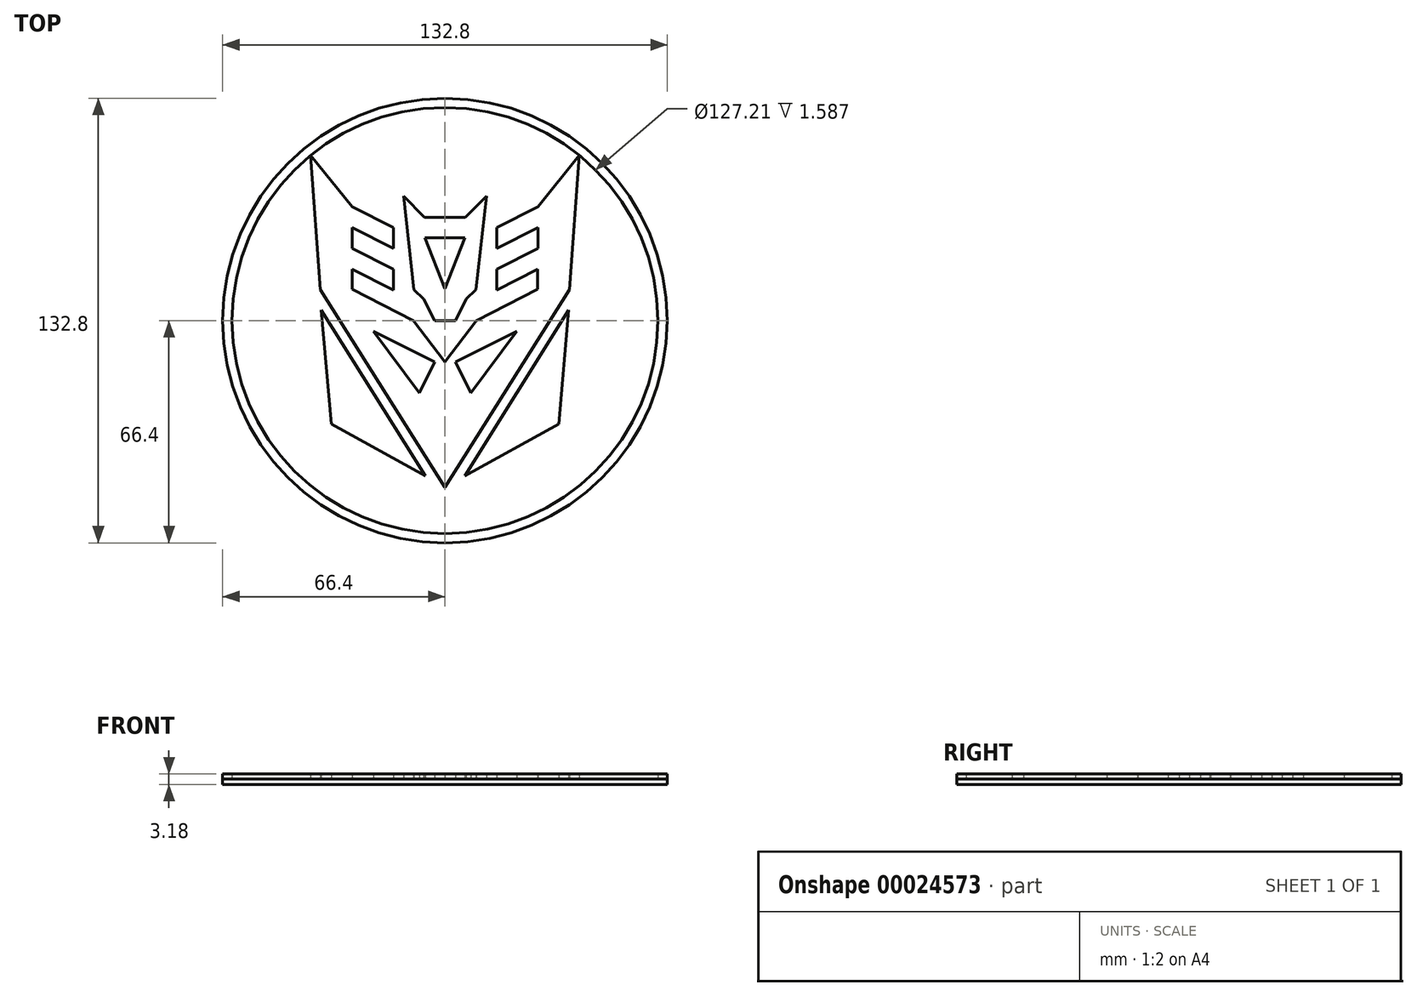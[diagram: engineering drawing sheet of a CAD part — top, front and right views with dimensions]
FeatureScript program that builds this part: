
annotation { "Feature Type Name" : "Feature", "Feature Type Description" : "" }
export const myFeature = defineFeature(function(context is Context, id is Id, definition is map)
    precondition{}
    {
        {
            var Q0;
            Q0=qCreatedBy(makeId("Top.planeOp"),FACE);
            var sketch = newSketch(context, id + "F0", { "sketchPlane" : qUnion([Q0])});
            skCircle(sketch, "E0", {"center": v(0, 0) * mm, "radius": 66.4 * mm});
            skSolve(sketch);
        }
        {
            var Q0;
            Q0 = qSketchRegion(id + "F0", true);
            extrude(context, id + "F1", {"entities" : qUnion([Q0]), "depth" : 1.59 * mm});
        }
        {
            var Q0;
            Q0=makeQuery(id+"F1.opExtrude","CAP_FACE",FACE,{"disambiguationData":[OSD([sQuery(id+"F0.wireOp",EDGE,"E0")])],"isStart":false});
            var sketch = newSketch(context, id + "F2", { "sketchPlane" : qUnion([Q0])});
            skLineSegment(sketch, "E1", {"start": v(-40.14, 49.34) * mm, "end": v(-27.72, 34) * mm});
            skLineSegment(sketch, "E2", {"start": v(-27.72, 34) * mm, "end": v(-15.4, 27.8) * mm});
            skLineSegment(sketch, "E3", {"start": v(-15.4, 27.8) * mm, "end": v(-15.4, 21.53) * mm});
            skLineSegment(sketch, "E4", {"start": v(-15.4, 21.53) * mm, "end": v(-27.77, 27.76) * mm});
            skLineSegment(sketch, "E5", {"start": v(-27.77, 27.76) * mm, "end": v(-27.77, 21.57) * mm});
            skLineSegment(sketch, "E6", {"start": v(-27.77, 21.57) * mm, "end": v(-15.4, 15.39) * mm});
            skLineSegment(sketch, "E7", {"start": v(-15.4, 15.39) * mm, "end": v(-15.4, 9.16) * mm});
            skLineSegment(sketch, "E8", {"start": v(-15.4, 9.16) * mm, "end": v(-27.68, 15.34) * mm});
            skLineSegment(sketch, "E9", {"start": v(-27.68, 15.34) * mm, "end": v(-27.68, 9.35) * mm});
            skLineSegment(sketch, "E10", {"start": v(-27.68, 9.35) * mm, "end": v(-9.4, 0) * mm});
            skLineSegment(sketch, "E11", {"start": v(-9.4, 0) * mm, "end": v(0, -12.37) * mm});
            skLineSegment(sketch, "E12", {"start": v(-40.14, 49.34) * mm, "end": v(-37.2, 9.23) * mm});
            skLineSegment(sketch, "E13", {"start": v(-37.2, 9.23) * mm, "end": v(0, -49.8) * mm});
            skLineSegment(sketch, "E14", {"start": v(-5.9, -46.44) * mm, "end": v(-36.98, 3.08) * mm});
            skLineSegment(sketch, "E15", {"start": v(-36.98, 3.08) * mm, "end": v(-33.96, -30.93) * mm});
            skLineSegment(sketch, "E16", {"start": v(-33.96, -30.93) * mm, "end": v(-5.9, -46.44) * mm});
            skLineSegment(sketch, "E17", {"start": v(-3.08, -12.32) * mm, "end": v(-21.39, -3.2) * mm});
            skLineSegment(sketch, "E18", {"start": v(-21.39, -3.2) * mm, "end": v(-7.68, -21.59) * mm});
            skLineSegment(sketch, "E19", {"start": v(-7.68, -21.59) * mm, "end": v(-3.08, -12.32) * mm});
            skLineSegment(sketch, "E20", {"start": v(0, 0) * mm, "end": v(-3.08, 0) * mm});
            skLineSegment(sketch, "E21", {"start": v(-3.08, 0) * mm, "end": v(-6.35, 6.44) * mm});
            skLineSegment(sketch, "E22", {"start": v(-6.35, 6.44) * mm, "end": v(-9.26, 9.26) * mm});
            skLineSegment(sketch, "E23", {"start": v(-9.26, 9.26) * mm, "end": v(-12.38, 37.13) * mm});
            skLineSegment(sketch, "E24", {"start": v(-12.38, 37.13) * mm, "end": v(-6.1, 30.82) * mm});
            skLineSegment(sketch, "E25", {"start": v(-6.1, 30.82) * mm, "end": v(0, 30.82) * mm});
            skLineSegment(sketch, "E26", {"start": v(0, 9.45) * mm, "end": v(-6, 24.67) * mm});
            skLineSegment(sketch, "E27", {"start": v(-6, 24.67) * mm, "end": v(0, 24.67) * mm});
            skLineSegment(sketch, "E28", {"start": v(0, 0) * mm, "end": v(0, 55.53) * mm, "construction": true});
            skLineSegment(sketch, "E29.MirrorCS", {"start": v(6.35, 6.44) * mm, "end": v(9.26, 9.26) * mm});
            skLineSegment(sketch, "E30.MirrorCS", {"start": v(0, 0) * mm, "end": v(3.08, 0) * mm});
            skLineSegment(sketch, "E31.MirrorCS", {"start": v(15.4, 15.39) * mm, "end": v(15.4, 9.16) * mm});
            skLineSegment(sketch, "E32.MirrorCS", {"start": v(15.4, 9.16) * mm, "end": v(27.68, 15.34) * mm});
            skLineSegment(sketch, "E33.MirrorCS", {"start": v(27.77, 21.57) * mm, "end": v(15.4, 15.39) * mm});
            skLineSegment(sketch, "E34.MirrorCS", {"start": v(27.77, 27.76) * mm, "end": v(27.77, 21.57) * mm});
            skLineSegment(sketch, "E35.MirrorCS", {"start": v(27.68, 15.34) * mm, "end": v(27.68, 9.35) * mm});
            skLineSegment(sketch, "E36.MirrorCS", {"start": v(15.4, 21.53) * mm, "end": v(27.77, 27.76) * mm});
            skLineSegment(sketch, "E37.MirrorCS", {"start": v(27.68, 9.35) * mm, "end": v(9.4, 0) * mm});
            skLineSegment(sketch, "E38.MirrorCS", {"start": v(15.4, 27.8) * mm, "end": v(15.4, 21.53) * mm});
            skLineSegment(sketch, "E39.MirrorCS", {"start": v(27.72, 34) * mm, "end": v(15.4, 27.8) * mm});
            skLineSegment(sketch, "E40.MirrorCS", {"start": v(9.4, 0) * mm, "end": v(0, -12.37) * mm});
            skLineSegment(sketch, "E41.MirrorCS", {"start": v(40.14, 49.34) * mm, "end": v(27.72, 34) * mm});
            skLineSegment(sketch, "E42.MirrorCS", {"start": v(33.96, -30.93) * mm, "end": v(5.9, -46.44) * mm});
            skLineSegment(sketch, "E43.MirrorCS", {"start": v(40.14, 49.34) * mm, "end": v(37.2, 9.23) * mm});
            skLineSegment(sketch, "E44.MirrorCS", {"start": v(0, 9.45) * mm, "end": v(6, 24.67) * mm});
            skLineSegment(sketch, "E45.MirrorCS", {"start": v(37.2, 9.23) * mm, "end": v(0, -49.8) * mm});
            skLineSegment(sketch, "E46.MirrorCS", {"start": v(12.38, 37.13) * mm, "end": v(6.1, 30.82) * mm});
            skLineSegment(sketch, "E47.MirrorCS", {"start": v(36.98, 3.08) * mm, "end": v(33.96, -30.93) * mm});
            skLineSegment(sketch, "E48.MirrorCS", {"start": v(5.9, -46.44) * mm, "end": v(36.98, 3.08) * mm});
            skLineSegment(sketch, "E49.MirrorCS", {"start": v(9.26, 9.26) * mm, "end": v(12.38, 37.13) * mm});
            skLineSegment(sketch, "E50.MirrorCS", {"start": v(3.08, 0) * mm, "end": v(6.35, 6.44) * mm});
            skLineSegment(sketch, "E51.MirrorCS", {"start": v(6, 24.67) * mm, "end": v(0, 24.67) * mm});
            skLineSegment(sketch, "E52.MirrorCS", {"start": v(7.68, -21.59) * mm, "end": v(3.08, -12.32) * mm});
            skLineSegment(sketch, "E53.MirrorCS", {"start": v(6.1, 30.82) * mm, "end": v(0, 30.82) * mm});
            skLineSegment(sketch, "E54.MirrorCS", {"start": v(21.39, -3.2) * mm, "end": v(7.68, -21.59) * mm});
            skLineSegment(sketch, "E55.MirrorCS", {"start": v(3.08, -12.32) * mm, "end": v(21.39, -3.2) * mm});
            skSolve(sketch);
        }
        {
            var Q0;
            Q0 = qSketchRegion(id + "F2", true);
            extrude(context, id + "F3", {"entities" : qUnion([Q0]), "operationType" : NewBodyOperationType.ADD, "depth" : 1.59 * mm});
        }
        {
            var Q0;
            {var subQ0=sQuery(id+"F0.wireOp",EDGE,"E0");Q0=makeQuery(id+"F3.boolean.opBoolean","SPLIT",FACE,{"disambiguationData":[TD([makeQuery(id+"F1.opExtrude","SWEPT_FACE",FACE,{"disambiguationData":[OSD([subQ0])]})])],"derivedFrom":makeQuery(id+"F1.opExtrude","CAP_FACE",FACE,{"disambiguationData":[OSD([subQ0])],"isStart":false})});}
            var sketch = newSketch(context, id + "F4", { "sketchPlane" : qUnion([Q0])});
            skCircle(sketch, "E56.0", {"center": v(0, 0) * mm, "radius": 66.4 * mm});
            skCircle(sketch, "E57", {"center": v(0, 0) * mm, "radius": 63.6 * mm});
            skSolve(sketch);
        }
        {
            var Q0;
            Q0 = qSketchRegion(id + "F4", true);
            extrude(context, id + "F5", {"entities" : qUnion([Q0]), "depth" : 1.59 * mm});
        }
    });
